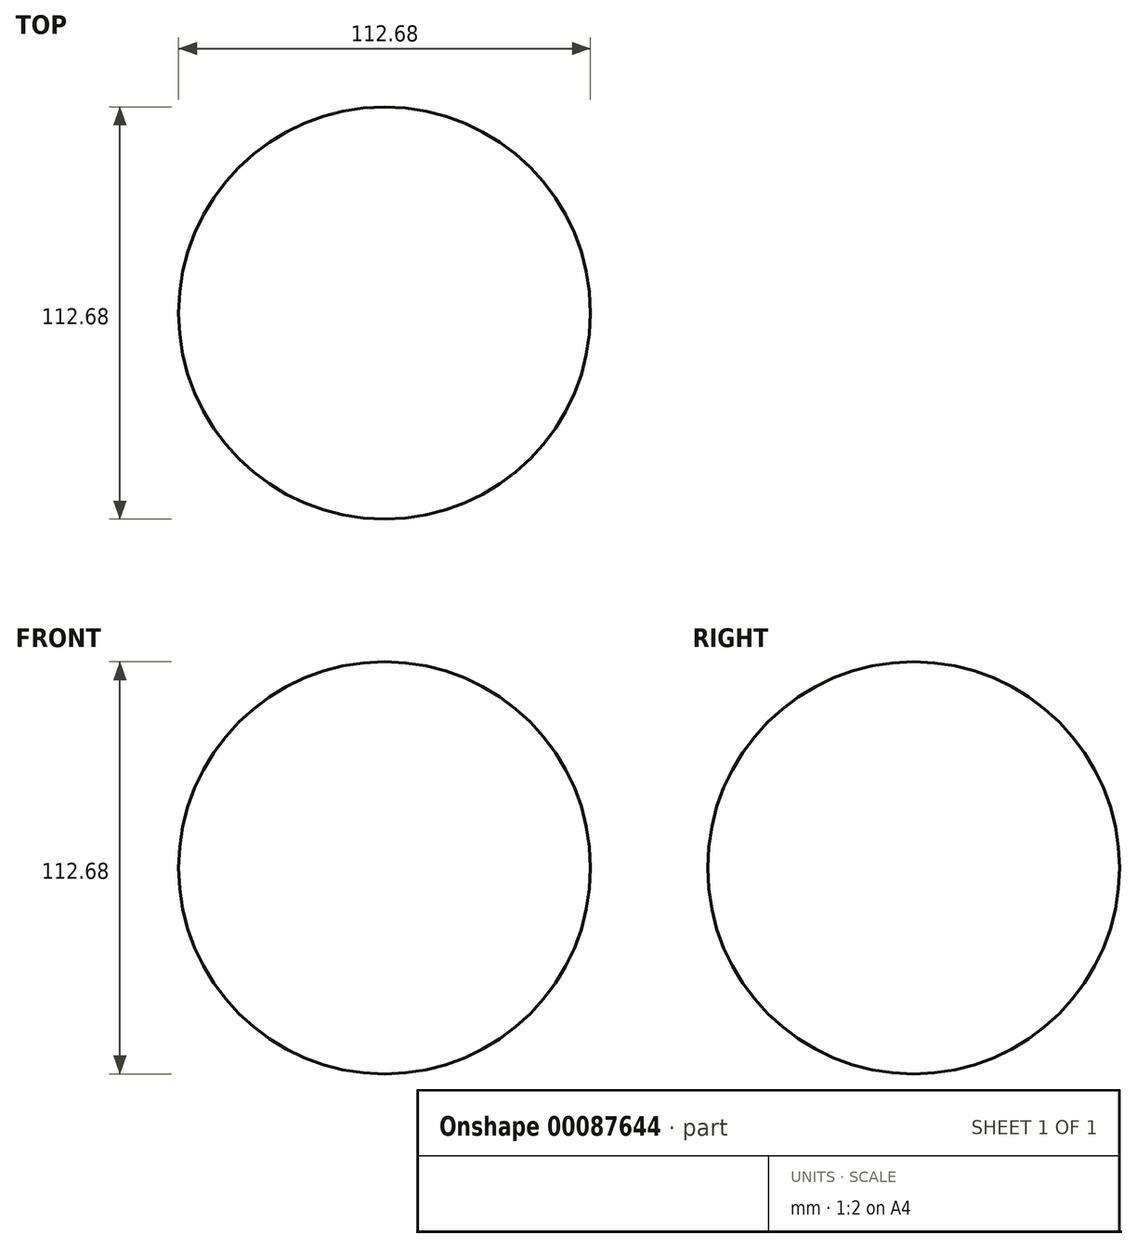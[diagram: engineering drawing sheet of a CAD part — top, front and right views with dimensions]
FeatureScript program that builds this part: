
annotation { "Feature Type Name" : "Feature", "Feature Type Description" : "" }
export const myFeature = defineFeature(function(context is Context, id is Id, definition is map)
    precondition{}
    {
        {
            var Q0;
            Q0=qCreatedBy(makeId("Front.planeOp"),FACE);
            var sketch = newSketch(context, id + "F0", { "sketchPlane" : qUnion([Q0])});
            skArc(sketch, "E0", {"start": v(0, -56.34) * mm, "mid": v(56.34, 0) * mm, "end": v(0, 56.34) * mm});
            skLineSegment(sketch, "E1", {"start": v(0, 56.34) * mm, "end": v(0, -56.34) * mm});
            skSolve(sketch);
        }
        {
            var Q0;
            Q0=makeQuery(id+"F0.imprint","IMPRINT",FACE,{"disambiguationData":[TD([[makeQuery(id+"F0.imprint","IMPRINT",EDGE,{"derivedFrom":sQuery(id+"F0.wireOp",EDGE,"E0")}),1.0]])]});
            var Q1;
            Q1=sQuery(id+"F0.wireOp",EDGE,"E1");
            revolve(context, id + "F1", {"entities" : qUnion([Q0]), "axis" : qUnion([Q1]), "revolveType" : RevolveType.FULL});
        }
        {
            var Q0;
            Q0=qCreatedBy(makeId("Front.planeOp"),FACE);
            cPlane(context, id + "F2", {"entities" : qUnion([Q0]), "cplaneType" : CPlaneType.OFFSET, "offset" : 38.1 * mm, "width" : 152.4 * mm, "height" : 152.4 * mm});
        }
        {
            var Q0;
            Q0=qCreatedBy(id+"F2.planeOp",FACE);
            cPlane(context, id + "F3", {"entities" : qUnion([Q0]), "cplaneType" : CPlaneType.OFFSET, "offset" : 12.7 * mm, "width" : 152.4 * mm, "height" : 152.4 * mm});
        }
    });
